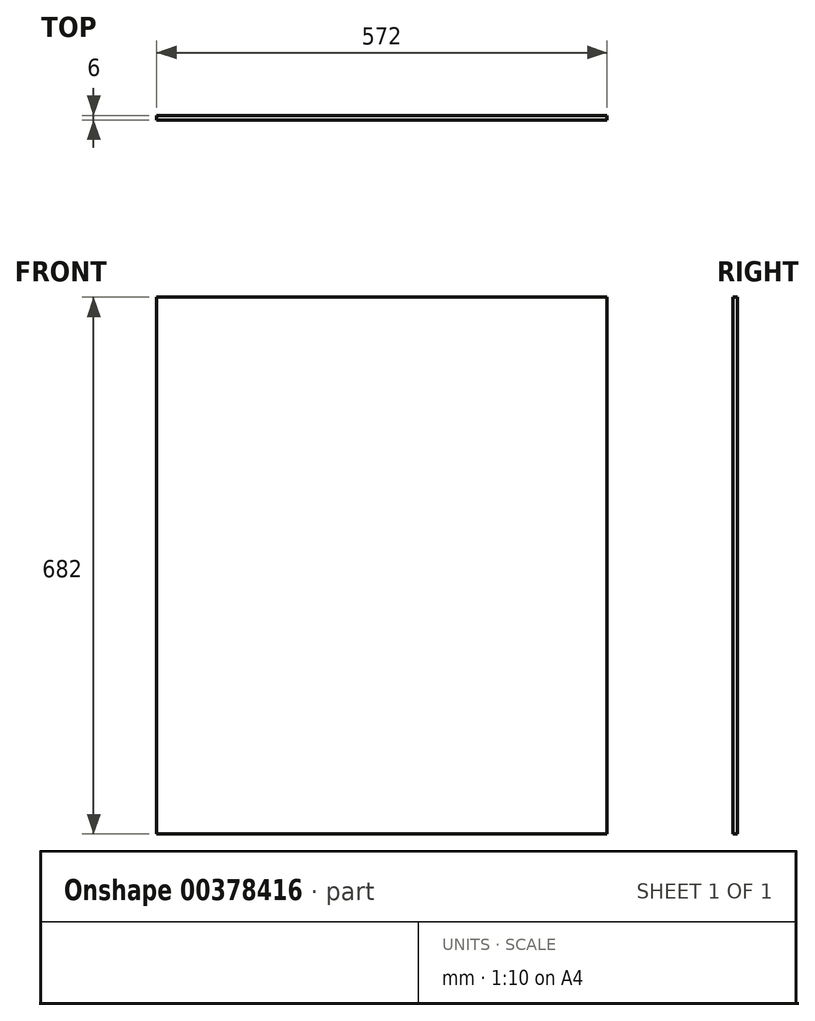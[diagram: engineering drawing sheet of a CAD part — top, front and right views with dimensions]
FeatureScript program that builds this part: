
annotation { "Feature Type Name" : "Feature", "Feature Type Description" : "" }
export const myFeature = defineFeature(function(context is Context, id is Id, definition is map)
    precondition{}
    {
        {
            var Q0;
            Q0=qCreatedBy(makeId("Front.planeOp"),FACE);
            var sketch = newSketch(context, id + "F0", { "sketchPlane" : qUnion([Q0])});
            skLineSegment(sketch, "E0.bottom", {"start": v(286, 341) * mm, "end": v(-286, 341) * mm});
            skLineSegment(sketch, "E0.top", {"start": v(286, -341) * mm, "end": v(-286, -341) * mm});
            skLineSegment(sketch, "E0.left", {"start": v(286, 341) * mm, "end": v(286, -341) * mm});
            skLineSegment(sketch, "E0.right", {"start": v(-286, 341) * mm, "end": v(-286, -341) * mm});
            skPoint(sketch, "E0.middle", {"position": v(0, 0) * mm});
            skSolve(sketch);
        }
        {
            var Q0;
            Q0=makeQuery(id+"F0.imprint","IMPRINT",FACE,{"disambiguationData":[TD([[makeQuery(id+"F0.imprint","IMPRINT",EDGE,{"derivedFrom":sQuery(id+"F0.wireOp",EDGE,"E0.bottom")}),1.0]])]});
            extrude(context, id + "F1", {"entities" : qUnion([Q0]), "depth" : 6 * mm});
        }
    });
